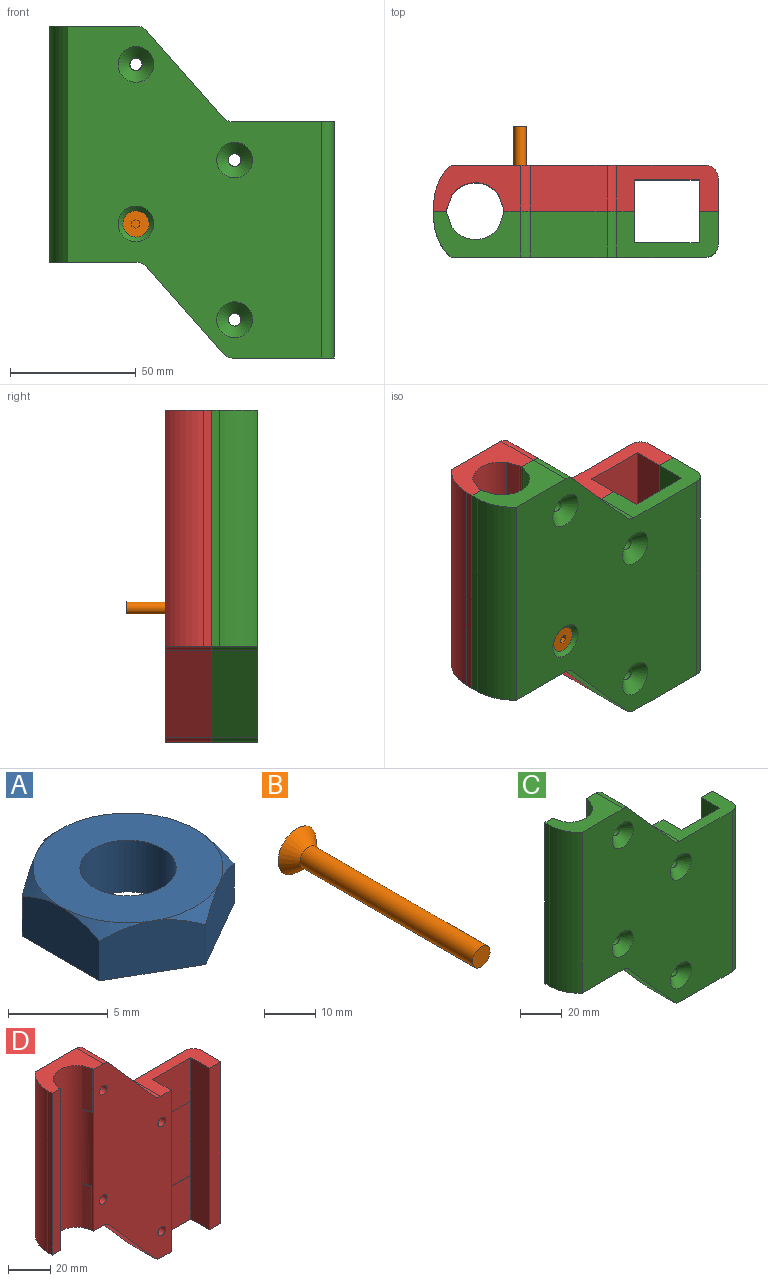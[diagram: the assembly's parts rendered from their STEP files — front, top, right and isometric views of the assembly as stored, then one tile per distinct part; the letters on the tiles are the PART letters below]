
ASSEMBLY  parts=4 mates=4
PART A: 15 faces, bbox 11.5x11.5x3.7 mm
  f0: plane 9.53x9.53mm, normal (0,0,1), area 53mm2, adj f8,f9,f10,f11,f12,f13,f14
  f1: plane 11x9.53mm, normal (0,0,-1), area 60.3mm2, adj f2,f3,f4,f5,f6,f7,f8
  f2: plane 5.3x3.72mm, normal (-0.5,0.87,0), area 16.1mm2, adj f1,f3,f7,f10,f14
  f3: plane 6.04x3.71mm, normal (-1,0,0), area 16.1mm2, adj f1,f2,f4,f13,f14
  f4: plane 5.3x3.72mm, normal (-0.5,-0.87,0), area 16.1mm2, adj f1,f3,f5,f12,f13
  f5: plane 5.3x3.72mm, normal (0.5,-0.87,0), area 16.1mm2, adj f1,f4,f6,f11,f12
  f6: plane 6.04x3.71mm, normal (1,0,0), area 16.1mm2, adj f1,f5,f7,f9,f11
  f7: plane 5.3x3.72mm, normal (0.5,0.87,0), area 16.1mm2, adj f1,f2,f6,f9,f10
  f8: cylinder r=2.41mm len=4.83mm, axis (0,0,-1), area 48.1mm2, adj f0,f1
  f9: cone r=4.76mm half-angle=45deg, axis (0,0,-1), area 2.7mm2, adj f0,f6,f7
  f10: cone r=4.76mm half-angle=45deg, axis (0,0,-1), area 2.7mm2, adj f0,f2,f7
  f11: cone r=4.76mm half-angle=45deg, axis (0,0,-1), area 2.7mm2, adj f0,f5,f6
  f12: cone r=4.76mm half-angle=45deg, axis (0,0,-1), area 2.7mm2, adj f0,f4,f5
  f13: cone r=4.76mm half-angle=45deg, axis (0,0,-1), area 2.7mm2, adj f0,f3,f4
  f14: cone r=4.76mm half-angle=45deg, axis (0,0,-1), area 2.7mm2, adj f0,f2,f3
PART B: 11 faces, bbox 10.4x50.8x10.4 mm
  f0: plane 10.44x10.44mm, normal (0,1,0), area 76.9mm2, adj f1,f4,f5,f6,f7,f8,f9
  f1: cone r=2.41mm half-angle=41deg, axis (0,1,0), area 102.6mm2, adj f0,f2
  f2: cylinder r=2.41mm len=47.57mm, axis (0,1,0), area 721.2mm2, adj f1,f3
  f3: plane 4.83x4.83mm, normal (0,-1,0), area 18.3mm2, adj f2
  f4: plane 1.83x1.68mm, normal (1,0,0), area 3.1mm2, adj f0,f5,f9,f10
  f5: plane 1.68x1.59mm, normal (0.5,0,0.87), area 3.1mm2, adj f0,f4,f6,f10
  f6: plane 1.68x1.59mm, normal (-0.5,0,0.87), area 3.1mm2, adj f0,f5,f7,f10
  f7: plane 1.83x1.68mm, normal (-1,0,0), area 3.1mm2, adj f0,f6,f8,f10
  f8: plane 1.68x1.59mm, normal (-0.5,0,-0.87), area 3.1mm2, adj f0,f7,f9,f10
  f9: plane 1.68x1.59mm, normal (0.5,0,-0.87), area 3.1mm2, adj f0,f4,f8,f10
  f10: plane 3.67x3.18mm, normal (0,1,0), area 8.7mm2, adj f4,f5,f6,f7,f8,f9
PART C: 42 faces, bbox 113.2x18.3x132.1 mm
  f0: plane 93.98x12.83mm, normal (-1,0,0), area 1186.1mm2, adj f9,f11,f17,f18,f38,f39,f40,f41
  f1: cylinder r=11.3mm len=93.98mm, axis (0,0,1), area 2758.9mm2, adj f2,f3,f5,f6,f25,f26,f27,f28
  f2: plane 34.54x18.29mm, normal (0,0,-1), area 401.3mm2, adj f1,f4,f5,f6,f7,f20,f21,f30
  f3: plane 34.54x18.29mm, normal (0,0,1), area 401.7mm2, adj f1,f4,f5,f6,f7,f20,f24,f25
  f4: plane 132.08x101.2mm, normal (0,-1,0), area 8874.9mm2, adj f2,f3,f8,f9,f11,f12,f20,f21
  f5: plane 132.08x52.07mm, normal (0,1,0), area 4812.5mm2, adj f1,f2,f3,f8,f9,f11,f12,f13
  f6: plane 93.98x5.21mm, normal (0,1,0), area 489.4mm2, adj f1,f2,f3,f7
  f7: plane 93.98x3.05mm, normal (-1,0,0), area 286.5mm2, adj f2,f3,f6,f20
  f8: plane 34.67x30.62mm, normal (-0.75,0,-0.66), area 845.9mm2, adj f4,f5,f21,f22
  f9: plane 40.38x18.29mm, normal (0,0,-1), area 413.7mm2, adj f0,f4,f5,f10,f17,f19,f22,f37
  f10: plane 93.98x13.21mm, normal (1,0,0), area 1241.3mm2, adj f9,f11,f17,f37
  f11: plane 40.38x18.29mm, normal (0,0,1), area 413.7mm2, adj f0,f4,f5,f10,f17,f19,f23,f37
  f12: plane 34.67x30.62mm, normal (0.75,0,0.66), area 845.9mm2, adj f4,f5,f23,f24
  f13: cylinder r=2.54mm len=13.72mm, axis (0,1,0), area 218.9mm2, adj f5,f35
  f14: cylinder r=2.54mm len=13.72mm, axis (0,1,0), area 218.9mm2, adj f5,f36
  f15: cylinder r=2.54mm len=13.72mm, axis (0,1,0), area 218.9mm2, adj f5,f34
  f16: cylinder r=2.54mm len=13.72mm, axis (0,1,0), area 218.9mm2, adj f5,f33
  f17: plane 93.98x7.62mm, normal (0,1,0), area 716.1mm2, adj f0,f9,f10,f11
  f18: plane 43.18x25.65mm, normal (0,1,0), area 1107.7mm2, adj f0,f19,f39,f41
  f19: plane 93.98x12.83mm, normal (1,0,0), area 1186.1mm2, adj f5,f9,f11,f18,f38,f39,f40,f41
  f20: cylinder r=20.32mm len=93.98mm, axis (0,0,1), area 1619.5mm2, adj f2,f3,f4,f7
  f21: cylinder r=5.08mm len=18.29mm, axis (0,-1,0), area 78.7mm2, adj f2,f4,f5,f8
  f22: cylinder r=5.08mm len=18.29mm, axis (0,1,0), area 78.7mm2, adj f4,f5,f8,f9
  f23: cylinder r=5.08mm len=18.29mm, axis (0,-1,0), area 78.7mm2, adj f4,f5,f11,f12
  f24: cylinder r=5.08mm len=18.29mm, axis (0,1,0), area 78.7mm2, adj f3,f4,f5,f12
  f25: plane 25.4x5.44mm, normal (0.94,0.34,0), area 147.1mm2, adj f1,f3,f26
  f26: plane 5.44x1.98mm, normal (0,0,-1), area 1.5mm2, adj f1,f25
  f27: plane 5.44x1.98mm, normal (0,0,-1), area 1.5mm2, adj f1,f28
  f28: plane 25.4x5.44mm, normal (-0.94,0.34,0), area 147.1mm2, adj f1,f3,f27
  f29: plane 5.12x1.91mm, normal (0,0,1), area 1.2mm2, adj f1,f30
  f30: plane 25.4x5.12mm, normal (0.94,0.35,0), area 138.8mm2, adj f1,f2,f29
  f31: plane 5.13x1.92mm, normal (0,0,1), area 1.2mm2, adj f1,f32
  f32: plane 25.4x5.13mm, normal (-0.94,0.35,0), area 139.1mm2, adj f1,f2,f31
  f33: cone r=2.54mm half-angle=45deg, axis (0,-1,0), area 196.1mm2, adj f4,f16
  f34: cone r=2.54mm half-angle=45deg, axis (0,-1,0), area 196.1mm2, adj f4,f15
  f35: cone r=2.54mm half-angle=45deg, axis (0,-1,0), area 196.1mm2, adj f4,f13
  f36: cone r=2.54mm half-angle=45deg, axis (0,-1,0), area 196.1mm2, adj f4,f14
  f37: cylinder r=5.08mm len=93.98mm, axis (0,0,-1), area 749.9mm2, adj f4,f9,f10,f11
  f38: plane 25.65x25.4mm, normal (0,1,0), area 651.6mm2, adj f0,f11,f19,f39
  f39: plane 25.65x0.38mm, normal (0,0,-1), area 9.8mm2, adj f0,f18,f19,f38
  f40: plane 25.65x25.4mm, normal (0,1,0), area 651.6mm2, adj f0,f9,f19,f41
  f41: plane 25.65x0.38mm, normal (0,0,1), area 9.8mm2, adj f0,f18,f19,f40
PART D: 74 faces, bbox 113.2x18.3x132.1 mm
  f0: cylinder r=2.54mm len=11.94mm, axis (0,-1,0), area 190.5mm2, adj f13,f72
  f1: cylinder r=2.54mm len=11.94mm, axis (0,-1,0), area 190.5mm2, adj f13,f73
  f2: cylinder r=2.54mm len=11.94mm, axis (0,-1,0), area 190.5mm2, adj f13,f70
  f3: cylinder r=2.54mm len=11.94mm, axis (0,-1,0), area 190.5mm2, adj f13,f71
  f4: cone r=2.54mm half-angle=45deg, axis (0,1,0), area 104.5mm2, adj f12,f63,f64,f65,f66,f67,f68
  f5: cone r=2.54mm half-angle=45deg, axis (0,1,0), area 104.5mm2, adj f12,f56,f57,f58,f59,f60,f61
  f6: cone r=2.54mm half-angle=45deg, axis (0,1,0), area 104.5mm2, adj f12,f49,f50,f51,f52,f53,f54
  f7: cone r=2.54mm half-angle=45deg, axis (0,1,0), area 104.5mm2, adj f12,f42,f43,f44,f45,f46,f47
  f8: plane 93.98x12.83mm, normal (-1,0,0), area 1186.1mm2, adj f17,f19,f21,f22,f38,f39,f40,f41
  f9: cylinder r=11.3mm len=93.98mm, axis (0,0,1), area 2758.9mm2, adj f10,f11,f13,f14,f29,f30,f31,f32
  f10: plane 34.54x18.29mm, normal (0,0,-1), area 401.3mm2, adj f9,f12,f13,f14,f15,f24,f25,f34
  f11: plane 34.54x18.29mm, normal (0,0,1), area 401.7mm2, adj f9,f12,f13,f14,f15,f24,f28,f29
  f12: plane 132.08x101.2mm, normal (0,1,0), area 8874.9mm2, adj f4,f5,f6,f7,f10,f11,f16,f17
  f13: plane 132.08x52.07mm, normal (0,-1,0), area 4812.5mm2, adj f0,f1,f2,f3,f9,f10,f11,f16
  f14: plane 93.98x5.21mm, normal (0,-1,0), area 489.4mm2, adj f9,f10,f11,f15
  f15: plane 93.98x3.05mm, normal (-1,0,0), area 286.5mm2, adj f10,f11,f14,f24
  f16: plane 34.67x30.62mm, normal (-0.75,0,-0.66), area 845.9mm2, adj f12,f13,f25,f26
  f17: plane 40.38x18.29mm, normal (0,0,-1), area 413.7mm2, adj f8,f12,f13,f18,f21,f23,f26,f37
  f18: plane 93.98x13.21mm, normal (1,0,0), area 1241.3mm2, adj f17,f19,f21,f37
  f19: plane 40.38x18.29mm, normal (0,0,1), area 413.7mm2, adj f8,f12,f13,f18,f21,f23,f27,f37
  f20: plane 34.67x30.62mm, normal (0.75,0,0.66), area 845.9mm2, adj f12,f13,f27,f28
  f21: plane 93.98x7.62mm, normal (0,-1,0), area 716.1mm2, adj f8,f17,f18,f19
  f22: plane 43.18x25.65mm, normal (0,-1,0), area 1107.7mm2, adj f8,f23,f39,f41
  f23: plane 93.98x12.83mm, normal (1,0,0), area 1186.1mm2, adj f13,f17,f19,f22,f38,f39,f40,f41
  f24: cylinder r=20.32mm len=93.98mm, axis (0,0,1), area 1619.5mm2, adj f10,f11,f12,f15
  f25: cylinder r=5.08mm len=18.29mm, axis (0,1,0), area 78.7mm2, adj f10,f12,f13,f16
  f26: cylinder r=5.08mm len=18.29mm, axis (0,-1,0), area 78.7mm2, adj f12,f13,f16,f17
  f27: cylinder r=5.08mm len=18.29mm, axis (0,1,0), area 78.7mm2, adj f12,f13,f19,f20
  f28: cylinder r=5.08mm len=18.29mm, axis (0,-1,0), area 78.7mm2, adj f11,f12,f13,f20
  f29: plane 25.4x5.44mm, normal (0.94,-0.34,0), area 147.1mm2, adj f9,f11,f30
  f30: plane 5.44x1.98mm, normal (0,0,-1), area 1.5mm2, adj f9,f29
  f31: plane 5.44x1.98mm, normal (0,0,-1), area 1.5mm2, adj f9,f32
  f32: plane 25.4x5.44mm, normal (-0.94,-0.34,0), area 147.1mm2, adj f9,f11,f31
  f33: plane 5.12x1.91mm, normal (0,0,1), area 1.2mm2, adj f9,f34
  f34: plane 25.4x5.12mm, normal (0.94,-0.35,0), area 138.8mm2, adj f9,f10,f33
  f35: plane 5.13x1.92mm, normal (0,0,1), area 1.2mm2, adj f9,f36
  f36: plane 25.4x5.13mm, normal (-0.94,-0.35,0), area 139.1mm2, adj f9,f10,f35
  f37: cylinder r=5.08mm len=93.98mm, axis (0,0,-1), area 749.9mm2, adj f12,f17,f18,f19
  f38: plane 25.65x25.4mm, normal (0,-1,0), area 651.6mm2, adj f8,f19,f23,f39
  f39: plane 25.65x0.38mm, normal (0,0,-1), area 9.8mm2, adj f8,f22,f23,f38
  f40: plane 25.65x25.4mm, normal (0,-1,0), area 651.6mm2, adj f8,f17,f23,f41
  f41: plane 25.65x0.38mm, normal (0,0,1), area 9.8mm2, adj f8,f22,f23,f40
  f42: plane 4.95x3.69mm, normal (-0.5,0,0.87), area 18.2mm2, adj f7,f43,f47,f48
  f43: plane 4.95x3.69mm, normal (0.5,0,0.87), area 18.2mm2, adj f7,f42,f44,f48
  f44: plane 5.73x3.69mm, normal (1,0,0), area 18.2mm2, adj f7,f43,f45,f48
  f45: plane 4.95x3.69mm, normal (0.5,0,-0.87), area 18.2mm2, adj f7,f44,f46,f48
  f46: plane 4.95x3.69mm, normal (-0.5,0,-0.87), area 18.2mm2, adj f7,f45,f47,f48
  f47: plane 5.73x3.69mm, normal (-1,0,0), area 18.2mm2, adj f7,f42,f46,f48
  f48: plane 11.44x9.91mm, normal (0,1,0), area 39.4mm2, adj f42,f43,f44,f45,f46,f47,f73
  f49: plane 4.95x3.69mm, normal (-0.5,0,0.87), area 18.2mm2, adj f6,f50,f54,f55
  f50: plane 4.95x3.69mm, normal (0.5,0,0.87), area 18.2mm2, adj f6,f49,f51,f55
  f51: plane 5.73x3.69mm, normal (1,0,0), area 18.2mm2, adj f6,f50,f52,f55
  f52: plane 4.95x3.69mm, normal (0.5,0,-0.87), area 18.2mm2, adj f6,f51,f53,f55
  f53: plane 4.95x3.69mm, normal (-0.5,0,-0.87), area 18.2mm2, adj f6,f52,f54,f55
  f54: plane 5.73x3.69mm, normal (-1,0,0), area 18.2mm2, adj f6,f49,f53,f55
  f55: plane 11.44x9.91mm, normal (0,1,0), area 39.4mm2, adj f49,f50,f51,f52,f53,f54,f72
  f56: plane 4.95x3.69mm, normal (-0.5,0,0.87), area 18.2mm2, adj f5,f57,f61,f62
  f57: plane 4.95x3.69mm, normal (0.5,0,0.87), area 18.2mm2, adj f5,f56,f58,f62
  f58: plane 5.73x3.69mm, normal (1,0,0), area 18.2mm2, adj f5,f57,f59,f62
  f59: plane 4.95x3.69mm, normal (0.5,0,-0.87), area 18.2mm2, adj f5,f58,f60,f62
  f60: plane 4.95x3.69mm, normal (-0.5,0,-0.87), area 18.2mm2, adj f5,f59,f61,f62
  f61: plane 5.73x3.69mm, normal (-1,0,0), area 18.2mm2, adj f5,f56,f60,f62
  f62: plane 11.44x9.91mm, normal (0,1,0), area 39.4mm2, adj f56,f57,f58,f59,f60,f61,f70
  f63: plane 4.95x3.69mm, normal (-0.5,0,0.87), area 18.2mm2, adj f4,f64,f68,f69
  f64: plane 4.95x3.69mm, normal (0.5,0,0.87), area 18.2mm2, adj f4,f63,f65,f69
  f65: plane 5.73x3.69mm, normal (1,0,0), area 18.2mm2, adj f4,f64,f66,f69
  f66: plane 4.95x3.69mm, normal (0.5,0,-0.87), area 18.2mm2, adj f4,f65,f67,f69
  f67: plane 4.95x3.69mm, normal (-0.5,0,-0.87), area 18.2mm2, adj f4,f66,f68,f69
  f68: plane 5.73x3.69mm, normal (-1,0,0), area 18.2mm2, adj f4,f63,f67,f69
  f69: plane 11.44x9.91mm, normal (0,1,0), area 39.4mm2, adj f63,f64,f65,f66,f67,f68,f71
  f70: cone r=2.54mm half-angle=45deg, axis (0,1,0), area 35.8mm2, adj f2,f62
  f71: cone r=2.54mm half-angle=45deg, axis (0,1,0), area 35.8mm2, adj f3,f69
  f72: cone r=2.54mm half-angle=45deg, axis (0,1,0), area 35.8mm2, adj f0,f55
  f73: cone r=2.54mm half-angle=45deg, axis (0,1,0), area 35.8mm2, adj f1,f48
PLACE A rot(axis=(-1,0,0),90deg) t=(17.78,13.21,92.54)mm
PLACE B rot(axis=(1,0,0),180deg) t=(17.78,-16.94,29.04)mm
PLACE C t=(0,0,-3.81)mm
PLACE D t=(0,0,-3.81)mm fixed
MATE cylindrical B.f1 <-> D.f2  axis (0,1,0) through (17.78,33.86,29.04)mm
MATE revolute A.f8 <-> D.f3  axis (0,-1,0) through (17.78,13.21,92.54)mm
MATE fastened C.f5 <-> D.f13  axis (0,1,0) through (11.3,0,107.78)mm
MATE fastened B.f1 <-> C.f15  axis (0,-1,0) through (17.78,-13.72,29.04)mm
